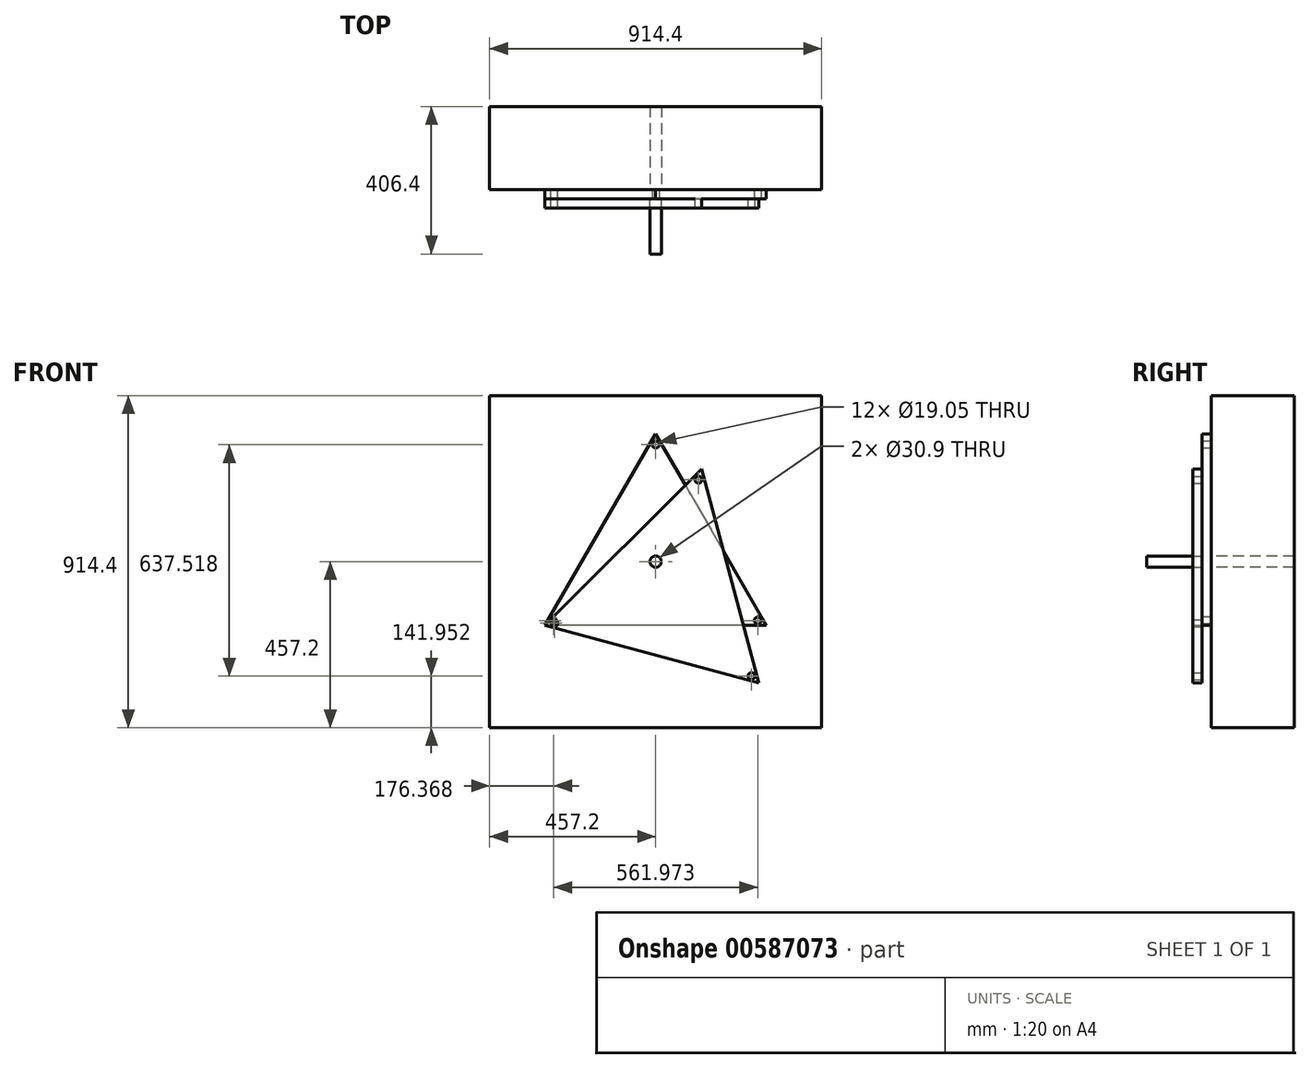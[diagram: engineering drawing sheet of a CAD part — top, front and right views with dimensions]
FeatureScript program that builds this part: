
annotation { "Feature Type Name" : "Feature", "Feature Type Description" : "" }
export const myFeature = defineFeature(function(context is Context, id is Id, definition is map)
    precondition{}
    {
        {
            var Q0;
            Q0=qCreatedBy(makeId("Front.planeOp"),FACE);
            var sketch = newSketch(context, id + "F0", { "sketchPlane" : qUnion([Q0])});
            skCircle(sketch, "E0.cCircle", {"center": v(0, 0) * mm, "radius": 175.98 * mm, "construction": true});
            skLineSegment(sketch, "E0.0", {"start": v(304.8, -175.98) * mm, "end": v(-304.8, -175.98) * mm});
            skLineSegment(sketch, "E0.1", {"start": v(-304.8, -175.98) * mm, "end": v(0, 351.95) * mm});
            skLineSegment(sketch, "E0.2", {"start": v(0, 351.95) * mm, "end": v(304.8, -175.98) * mm});
            skPoint(sketch, "E0.0.midPoint", {"position": v(0, -175.98) * mm});
            skLineSegment(sketch, "E1.bottom", {"start": v(-457.2, -457.2) * mm, "end": v(457.2, -457.2) * mm});
            skLineSegment(sketch, "E1.top", {"start": v(-457.2, 457.2) * mm, "end": v(457.2, 457.2) * mm});
            skLineSegment(sketch, "E1.left", {"start": v(-457.2, -457.2) * mm, "end": v(-457.2, 457.2) * mm});
            skLineSegment(sketch, "E1.right", {"start": v(457.2, -457.2) * mm, "end": v(457.2, 457.2) * mm});
            skCircle(sketch, "E2", {"center": v(-280.83, -162.14) * mm, "radius": 9.53 * mm});
            skCircle(sketch, "E3", {"center": v(281.14, -162.32) * mm, "radius": 9.53 * mm});
            skCircle(sketch, "E4", {"center": v(0, 322.27) * mm, "radius": 9.53 * mm});
            skLineSegment(sketch, "E5", {"start": v(0, 0) * mm, "end": v(-304.8, -175.98) * mm, "construction": true});
            skLineSegment(sketch, "E6", {"start": v(0, 0) * mm, "end": v(304.8, -175.98) * mm, "construction": true});
            skSolve(sketch);
        }
        {
            var Q0;
            Q0=makeQuery(id+"F0.imprint","IMPRINT",FACE,{"disambiguationData":[TD([[makeQuery(id+"F0.imprint","IMPRINT",EDGE,{"derivedFrom":sQuery(id+"F0.wireOp",EDGE,"E0.0")}),1.0]])]});
            var sketch = newSketch(context, id + "F1", { "sketchPlane" : qUnion([Q0])});
            skCircle(sketch, "E7.cCircle", {"center": v(0, 0) * mm, "radius": 175.98 * mm, "construction": true});
            skLineSegment(sketch, "E7.0", {"start": v(284.03, -333.75) * mm, "end": v(-304.8, -175.98) * mm});
            skLineSegment(sketch, "E7.1", {"start": v(-304.8, -175.98) * mm, "end": v(126.25, 255.08) * mm});
            skLineSegment(sketch, "E7.2", {"start": v(126.25, 255.08) * mm, "end": v(284.03, -333.75) * mm});
            skPoint(sketch, "E8", {"position": v(-304.8, -175.98) * mm});
            skCircle(sketch, "E9", {"center": v(-278.77, -169.63) * mm, "radius": 9.53 * mm});
            skCircle(sketch, "E10", {"center": v(264.01, -315.25) * mm, "radius": 9.53 * mm});
            skCircle(sketch, "E11", {"center": v(117.87, 225.6) * mm, "radius": 9.53 * mm});
            skSolve(sketch);
        }
        {
            var Q0;
            Q0=makeQuery(id+"F0.imprint","IMPRINT",FACE,{"disambiguationData":[TD([[makeQuery(id+"F0.imprint","IMPRINT",EDGE,{"derivedFrom":sQuery(id+"F0.wireOp",EDGE,"E0.0")}),-1.0]])]});
            extrude(context, id + "F2", {"entities" : qUnion([Q0]), "oppositeDirection" : true, "depth" : 25.4 * mm, "offsetDistance" : 25.4 * mm});
        }
        {
            var Q0;
            Q0 = qSketchRegion(id + "F1", true);
            extrude(context, id + "F3", {"entities" : qUnion([Q0]), "depth" : 25.4 * mm, "offsetDistance" : 25.4 * mm});
        }
        {
            var Q0;
            Q0=qCreatedBy(makeId("Front.planeOp"),FACE);
            var sketch = newSketch(context, id + "F4", { "sketchPlane" : qUnion([Q0])});
            skLineSegment(sketch, "E12.bottom", {"start": v(-457.2, -457.2) * mm, "end": v(457.2, -457.2) * mm});
            skLineSegment(sketch, "E12.top", {"start": v(-457.2, 457.2) * mm, "end": v(457.2, 457.2) * mm});
            skLineSegment(sketch, "E12.left", {"start": v(-457.2, -457.2) * mm, "end": v(-457.2, 457.2) * mm});
            skLineSegment(sketch, "E12.right", {"start": v(457.2, -457.2) * mm, "end": v(457.2, 457.2) * mm});
            skPoint(sketch, "E12.middle", {"position": v(0, 0) * mm});
            skCircle(sketch, "E13", {"center": v(0, 0) * mm, "radius": 15.45 * mm});
            skSolve(sketch);
        }
        {
            var Q0;
            Q0 = qSketchRegion(id + "F4", true);
            extrude(context, id + "F5", {"entities" : qUnion([Q0]), "oppositeDirection" : true, "depth" : 254 * mm, "offsetDistance" : 25.4 * mm, "hasSecondDirection" : true, "secondDirectionOppositeDirection" : true, "secondDirectionDepth" : 25.4 * mm});
        }
        {
            var Q0;
            Q0=makeQuery(id+"F4.imprint","IMPRINT",FACE,{"disambiguationData":[TD([[makeQuery(id+"F4.imprint","IMPRINT",EDGE,{"derivedFrom":sQuery(id+"F4.wireOp",EDGE,"E13")}),1.0]])]});
            extrude(context, id + "F6", {"entities" : qUnion([Q0]), "depth" : 152.4 * mm, "offsetDistance" : 25.4 * mm});
        }
    });
